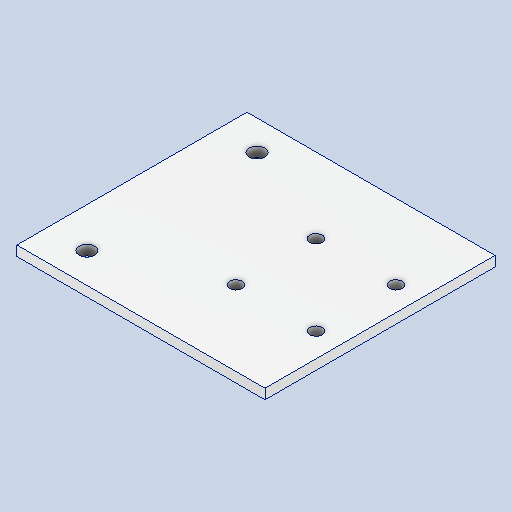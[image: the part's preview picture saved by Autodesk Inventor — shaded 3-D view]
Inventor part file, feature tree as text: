
AUTODESK INVENTOR PART (.ipt)
format: ipt  version: 2023 (Build 270158000, 158)  size: 156,672 bytes
history: native  units: in
note: dims shown in document units (in); Inventor stores cm internally (conversion verified against a paired STEP export)
features: extrude x3, sketch x2, projected_geometry x1
ambient origin geometry x8: Origin, YZ Plane, XZ Plane, XY Plane, X Axis, Y Axis, Z Axis, Center Point
bodies: Solid1 (feature_tree)
feature tree (6):
  extrude  "Extrusion1"  Depth=1.875in
  sketch  "Sketch2"  dims[d2=0.1969in d3=0.1969in d4=0.5in d5=0.5in d6=0.375in d7=0.375in d8=1.0in d9=1.0in d10=1.0in d11=1.0in d12=0.159in d13=0.159in d14=0.159in d15=0.159in d16=0.4375in d17=0.125in d18=0.0in d19=3.1in d20=0.375in d21=0.5in d22=0.5in d23=0.375in d24=0.5in d25=0.5in d26=0.125in d27=0.0in d28=0.0in d29=0.0in]
  extrude  "Extrusion2"  Depth=0.125in
  extrude  "Extrusion3"  Depth=0.125in
  sketch  "Sketch1"  dims[d0=4.0in d1=1.875in]
  projected_geometry  "Projected Loop1"
